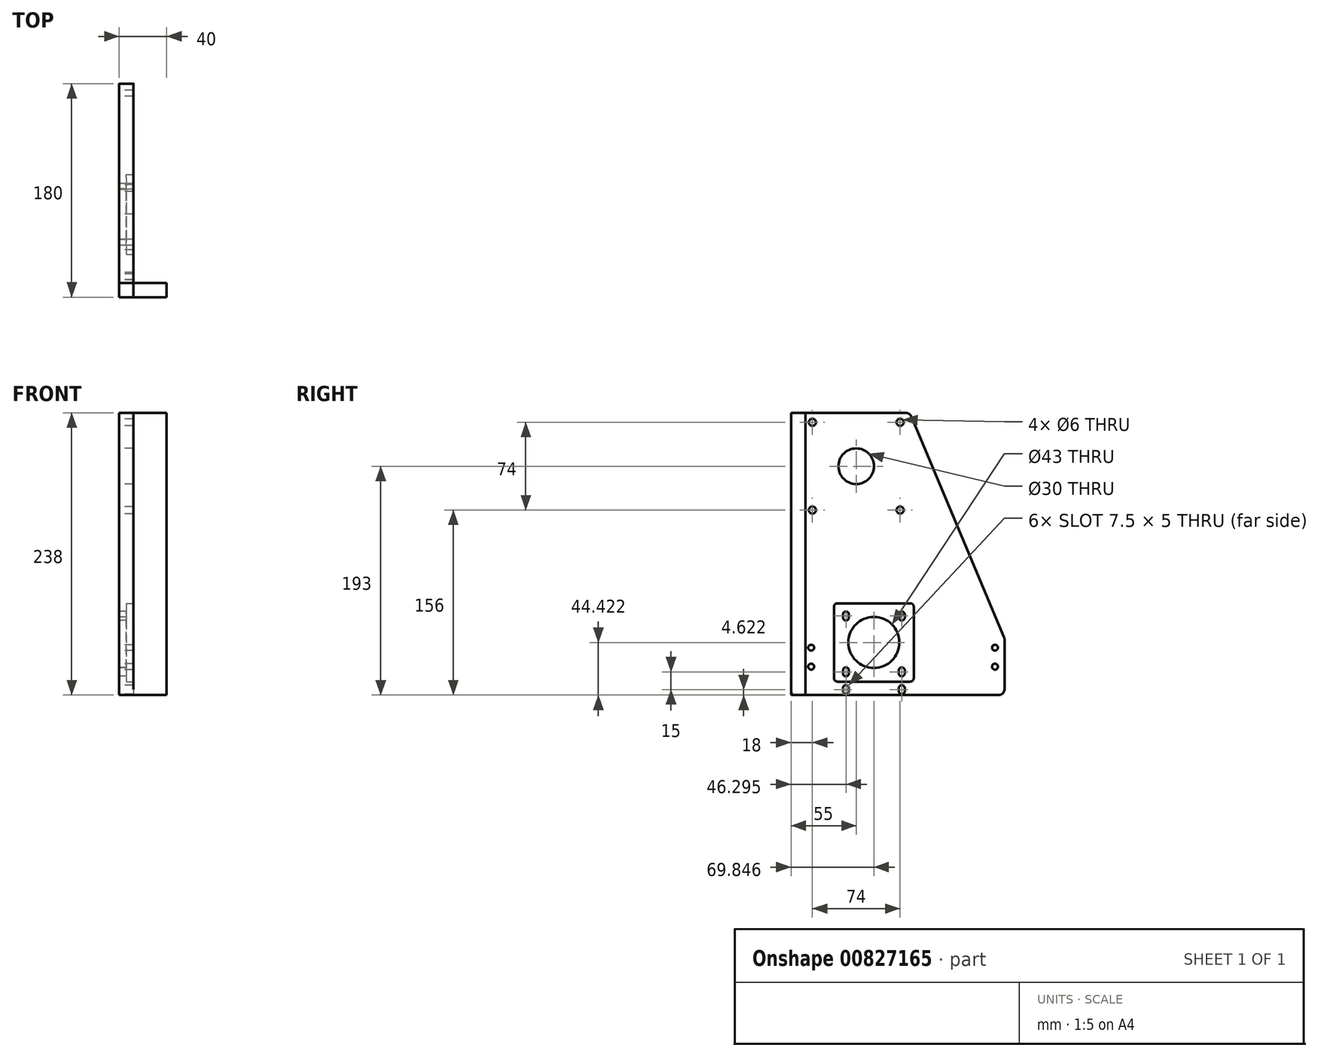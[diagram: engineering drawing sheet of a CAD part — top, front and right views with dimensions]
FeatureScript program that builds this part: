
annotation { "Feature Type Name" : "Feature", "Feature Type Description" : "" }
export const myFeature = defineFeature(function(context is Context, id is Id, definition is map)
    precondition{}
    {
        {
            var Q0;
            Q0=qCreatedBy(makeId("Right.planeOp"),FACE);
            var sketch = newSketch(context, id + "F0", { "sketchPlane" : qUnion([Q0])});
            skLineSegment(sketch, "E0", {"start": v(-40, 70) * mm, "end": v(-40, -155) * mm});
            skLineSegment(sketch, "E1", {"start": v(140, -168) * mm, "end": v(140, -120) * mm});
            skLineSegment(sketch, "E2", {"start": v(140, -120) * mm, "end": v(60, 70) * mm});
            skLineSegment(sketch, "E3", {"start": v(-40, 70) * mm, "end": v(60, 70) * mm});
            skLineSegment(sketch, "E4", {"start": v(0.37, 70) * mm, "end": v(-40, 70) * mm, "construction": true});
            skLineSegment(sketch, "E5", {"start": v(-153.96, -155) * mm, "end": v(265.91, -155) * mm, "construction": true});
            skLineSegment(sketch, "E6.top", {"start": v(6.3, -147.13) * mm, "end": v(53.4, -147.13) * mm, "construction": true});
            skLineSegment(sketch, "E7", {"start": v(29.85, -123.58) * mm, "end": v(29.85, -139.58) * mm, "construction": true});
            skLineSegment(sketch, "E8.bottom", {"start": v(60, 70) * mm, "end": v(-30, 70) * mm, "construction": true});
            skLineSegment(sketch, "E8.top", {"start": v(60, -20) * mm, "end": v(-30, -20) * mm, "construction": true});
            skLineSegment(sketch, "E8.left", {"start": v(60, 70) * mm, "end": v(60, -20) * mm, "construction": true});
            skLineSegment(sketch, "E8.right", {"start": v(-30, 70) * mm, "end": v(-30, -20) * mm, "construction": true});
            skLineSegment(sketch, "E9", {"start": v(-30, 70) * mm, "end": v(-30, 62) * mm, "construction": true});
            skLineSegment(sketch, "E10", {"start": v(-30, 62) * mm, "end": v(-22, 62) * mm, "construction": true});
            skCircle(sketch, "E11", {"center": v(-22, 62) * mm, "radius": 3 * mm});
            skCircle(sketch, "E12.0.1.0", {"center": v(-22, -12) * mm, "radius": 3 * mm});
            skCircle(sketch, "E12.1.0.0", {"center": v(52, 62) * mm, "radius": 3 * mm});
            skCircle(sketch, "E12.1.1.0", {"center": v(52, -12) * mm, "radius": 3 * mm});
            skLineSegment(sketch, "E12.direction1", {"start": v(-22, 62) * mm, "end": v(52, 62) * mm, "construction": true});
            skLineSegment(sketch, "E12.direction2", {"start": v(-22, 62) * mm, "end": v(-22, -12) * mm, "construction": true});
            skLineSegment(sketch, "E13", {"start": v(0, 0) * mm, "end": v(-30, 0) * mm, "construction": true});
            skLineSegment(sketch, "E14", {"start": v(-30, -20) * mm, "end": v(-30, 0) * mm, "construction": true});
            skLineSegment(sketch, "E15.bottom", {"start": v(-15.26, 54.8) * mm, "end": v(45.26, 54.8) * mm, "construction": true});
            skLineSegment(sketch, "E15.top", {"start": v(-15.26, -4.8) * mm, "end": v(45.26, -4.8) * mm, "construction": true});
            skLineSegment(sketch, "E15.left", {"start": v(-15.26, 54.8) * mm, "end": v(-15.26, -4.8) * mm, "construction": true});
            skLineSegment(sketch, "E15.right", {"start": v(45.26, 54.8) * mm, "end": v(45.26, -4.8) * mm, "construction": true});
            skLineSegment(sketch, "E16", {"start": v(0, 0) * mm, "end": v(0.37, 70) * mm, "construction": true});
            skLineSegment(sketch, "E17", {"start": v(52, -12) * mm, "end": v(-22, 62) * mm, "construction": true});
            skCircle(sketch, "E18", {"center": v(15, 25) * mm, "radius": 15 * mm});
            skLineSegment(sketch, "E19.bottom", {"start": v(-15.28, -29.16) * mm, "end": v(80.04, -29.16) * mm});
            skLineSegment(sketch, "E19.top", {"start": v(-15.28, -109.16) * mm, "end": v(113.72, -109.16) * mm});
            skLineSegment(sketch, "E19.left", {"start": v(-15.28, -29.16) * mm, "end": v(-15.28, -109.16) * mm});
            skLineSegment(sketch, "E20", {"start": v(80.04, -29.16) * mm, "end": v(113.72, -109.16) * mm});
            skLineSegment(sketch, "E21", {"start": v(132, -122.13) * mm, "end": v(132, -167.13) * mm, "construction": true});
            skLineSegment(sketch, "E22", {"start": v(132, -155) * mm, "end": v(132, -144) * mm, "construction": true});
            skCircle(sketch, "E23", {"center": v(132, -144) * mm, "radius": 11 * mm, "construction": true});
            skCircle(sketch, "E24", {"center": v(132, -144) * mm, "radius": 2.5 * mm});
            skLineSegment(sketch, "E25", {"start": v(132, -144) * mm, "end": v(132, -128) * mm, "construction": true});
            skCircle(sketch, "E26", {"center": v(132, -128) * mm, "radius": 2.5 * mm});
            skLineSegment(sketch, "E27", {"start": v(140, -155) * mm, "end": v(132, -155) * mm, "construction": true});
            skLineSegment(sketch, "E28", {"start": v(-40, -155) * mm, "end": v(-23, -155) * mm, "construction": true});
            skLineSegment(sketch, "E29", {"start": v(-23, -155) * mm, "end": v(-23, -144) * mm, "construction": true});
            skLineSegment(sketch, "E30", {"start": v(-23, -122.13) * mm, "end": v(-23, -167.13) * mm, "construction": true});
            skCircle(sketch, "E31", {"center": v(-23, -144) * mm, "radius": 11 * mm, "construction": true});
            skCircle(sketch, "E32", {"center": v(-23, -144) * mm, "radius": 2.5 * mm});
            skLineSegment(sketch, "E33", {"start": v(-23, -144) * mm, "end": v(-23, -128) * mm, "construction": true});
            skCircle(sketch, "E34", {"center": v(-23, -128) * mm, "radius": 2.5 * mm});
            skLineSegment(sketch, "E35", {"start": v(265.91, -188) * mm, "end": v(-153.96, -188) * mm, "construction": true});
            skLineSegment(sketch, "E36", {"start": v(140, -188) * mm, "end": v(140, -176) * mm, "construction": true});
            skLineSegment(sketch, "E37", {"start": v(265.91, -176) * mm, "end": v(-153.96, -176) * mm, "construction": true});
            skLineSegment(sketch, "E38", {"start": v(-19.95, -188) * mm, "end": v(100.05, -188) * mm});
            skLineSegment(sketch, "E39", {"start": v(-153.96, -123.47) * mm, "end": v(-153.96, -187.78) * mm, "construction": true});
            skLineSegment(sketch, "E40", {"start": v(265.91, -147.12) * mm, "end": v(265.91, -199.13) * mm, "construction": true});
            skLineSegment(sketch, "E41", {"start": v(140, -155) * mm, "end": v(140, -168) * mm});
            skLineSegment(sketch, "E42", {"start": v(140, -168) * mm, "end": v(-40, -168) * mm});
            skLineSegment(sketch, "E43", {"start": v(-40, -155) * mm, "end": v(-40, -168) * mm});
            skCircle(sketch, "E44", {"center": v(6.3, -147.13) * mm, "radius": 2.5 * mm});
            skCircle(sketch, "E45", {"center": v(53.4, -147.13) * mm, "radius": 2.5 * mm});
            skCircle(sketch, "E46", {"center": v(29.85, -123.58) * mm, "radius": 21.5 * mm});
            skLineSegment(sketch, "E47.bottom", {"start": v(6.3, -100.03) * mm, "end": v(53.4, -100.03) * mm, "construction": true});
            skLineSegment(sketch, "E47.left", {"start": v(6.3, -100.03) * mm, "end": v(6.3, -147.13) * mm, "construction": true});
            skLineSegment(sketch, "E47.right", {"start": v(53.4, -100.03) * mm, "end": v(53.4, -147.13) * mm, "construction": true});
            skCircle(sketch, "E48", {"center": v(29.85, -123.58) * mm, "radius": 6.5 * mm, "construction": true});
            skLineSegment(sketch, "E49", {"start": v(6.3, -100.03) * mm, "end": v(53.4, -147.13) * mm, "construction": true});
            skArc(sketch, "E50", {"start": v(3.8, -102.53) * mm, "mid": v(6.3, -105.03) * mm, "end": v(8.8, -102.53) * mm});
            skLineSegment(sketch, "E51", {"start": v(3.8, -100.03) * mm, "end": v(3.8, -102.53) * mm});
            skLineSegment(sketch, "E52", {"start": v(8.8, -100.03) * mm, "end": v(8.8, -102.53) * mm});
            skArc(sketch, "E53.trimOffspring", {"start": v(8.8, -100.03) * mm, "mid": v(6.3, -97.53) * mm, "end": v(3.8, -100.03) * mm});
            skArc(sketch, "E54", {"start": v(50.88, -102.52) * mm, "mid": v(53.38, -105.02) * mm, "end": v(55.88, -102.52) * mm});
            skLineSegment(sketch, "E55", {"start": v(50.88, -100.02) * mm, "end": v(50.88, -102.52) * mm});
            skLineSegment(sketch, "E56", {"start": v(55.88, -100.02) * mm, "end": v(55.88, -102.52) * mm});
            skArc(sketch, "E57.trimOffspring", {"start": v(55.88, -100.02) * mm, "mid": v(53.38, -97.52) * mm, "end": v(50.88, -100.02) * mm});
            skArc(sketch, "E58", {"start": v(50.9, -149.63) * mm, "mid": v(53.4, -152.13) * mm, "end": v(55.9, -149.63) * mm});
            skLineSegment(sketch, "E59", {"start": v(50.9, -147.13) * mm, "end": v(50.9, -149.63) * mm});
            skLineSegment(sketch, "E60", {"start": v(55.9, -147.13) * mm, "end": v(55.9, -149.63) * mm});
            skArc(sketch, "E61.trimOffspring", {"start": v(55.9, -147.13) * mm, "mid": v(53.4, -144.63) * mm, "end": v(50.9, -147.13) * mm});
            skArc(sketch, "E62", {"start": v(3.8, -149.63) * mm, "mid": v(6.3, -152.13) * mm, "end": v(8.8, -149.63) * mm});
            skLineSegment(sketch, "E63", {"start": v(3.8, -147.13) * mm, "end": v(3.8, -149.63) * mm});
            skLineSegment(sketch, "E64", {"start": v(8.8, -147.13) * mm, "end": v(8.8, -149.63) * mm});
            skArc(sketch, "E65.trimOffspring", {"start": v(8.8, -147.13) * mm, "mid": v(6.3, -144.63) * mm, "end": v(3.8, -147.13) * mm});
            skLineSegment(sketch, "E66", {"start": v(29.85, -123.58) * mm, "end": v(29.85, -126.08) * mm, "construction": true});
            skCircle(sketch, "E67", {"center": v(6.3, -147.13) * mm, "radius": 15 * mm, "construction": true});
            skCircle(sketch, "E68", {"center": v(53.4, -147.13) * mm, "radius": 15 * mm, "construction": true});
            skPoint(sketch, "E69.visualSharp", {"position": v(-0.7, -166.75) * mm});
            skPoint(sketch, "E70.visualSharp", {"position": v(59.3, -166.75) * mm});
            skArc(sketch, "E71", {"start": v(3.8, -164.63) * mm, "mid": v(6.3, -167.13) * mm, "end": v(8.8, -164.63) * mm});
            skLineSegment(sketch, "E72", {"start": v(3.8, -162.13) * mm, "end": v(3.8, -164.63) * mm});
            skLineSegment(sketch, "E73", {"start": v(8.8, -162.13) * mm, "end": v(8.8, -164.63) * mm});
            skArc(sketch, "E74.trimOffspring", {"start": v(8.8, -162.13) * mm, "mid": v(6.3, -159.63) * mm, "end": v(3.8, -162.13) * mm});
            skArc(sketch, "E75", {"start": v(50.9, -164.63) * mm, "mid": v(53.4, -167.13) * mm, "end": v(55.9, -164.63) * mm});
            skLineSegment(sketch, "E76", {"start": v(50.9, -162.13) * mm, "end": v(50.9, -164.63) * mm});
            skLineSegment(sketch, "E77", {"start": v(55.9, -162.13) * mm, "end": v(55.9, -164.63) * mm});
            skArc(sketch, "E78.trimOffspring", {"start": v(55.9, -162.13) * mm, "mid": v(53.4, -159.63) * mm, "end": v(50.9, -162.13) * mm});
            skLineSegment(sketch, "E79", {"start": v(55.9, -147.13) * mm, "end": v(55.9, -162.13) * mm, "construction": true});
            skLineSegment(sketch, "E80", {"start": v(23.35, -123.47) * mm, "end": v(22.64, -166.43) * mm, "construction": true});
            skLineSegment(sketch, "E81", {"start": v(36.34, -123.3) * mm, "end": v(36.34, -166.03) * mm, "construction": true});
            skSolve(sketch);
        }
        {
            var Q0;
            Q0=makeQuery(id+"F0.imprint","IMPRINT",FACE,{"disambiguationData":[TD([[makeQuery(id+"F0.imprint","IMPRINT",EDGE,{"derivedFrom":sQuery(id+"F0.wireOp",EDGE,"E0")}),1.0]])]});
            var Q1;
            Q1=makeQuery(id+"F0.imprint","IMPRINT",FACE,{"disambiguationData":[TD([[makeQuery(id+"F0.imprint","IMPRINT",EDGE,{"derivedFrom":sQuery(id+"F0.wireOp",EDGE,"E19.bottom")}),-1.0]])]});
            extrude(context, id + "F1", {"entities" : qUnion([Q0, Q1]), "depth" : 12 * mm, "offsetDistance" : 25 * mm});
        }
        {
            var Q0;
            Q0=makeQuery(id+"F1.opExtrude","SWEPT_EDGE",EDGE,{"disambiguationData":[OSD([sQuery(id+"F0.wireOp",EDGE,"E2"),sQuery(id+"F0.wireOp",EDGE,"E3")])]});
            var Q1;
            Q1=makeQuery(id+"F1.opExtrude","SWEPT_EDGE",EDGE,{"disambiguationData":[OSD([sQuery(id+"F0.wireOp",EDGE,"E1"),sQuery(id+"F0.wireOp",EDGE,"E2")])]});
            var Q2;
            Q2=makeQuery(id+"F1.opExtrude","SWEPT_EDGE",EDGE,{"disambiguationData":[OSD([sQuery(id+"F0.wireOp",EDGE,"E41"),sQuery(id+"F0.wireOp",EDGE,"E42")])]});
            fillet(context, id + "F2", {"entities" : qUnion([Q0, Q1, Q2]), "radius" : 5 * mm, "tangentPropagation" : true, "allowEdgeOverflow" : false});
        }
        {
            var Q0;
            Q0=qCreatedBy(makeId("Right.planeOp"),FACE);
            var sketch = newSketch(context, id + "F3", { "sketchPlane" : qUnion([Q0])});
            skLineSegment(sketch, "E82.bottom", {"start": v(-40, 70) * mm, "end": v(-28, 70) * mm});
            skLineSegment(sketch, "E82.top", {"start": v(-40, -168) * mm, "end": v(-28, -168) * mm});
            skLineSegment(sketch, "E82.left", {"start": v(-28, 70) * mm, "end": v(-28, -168) * mm});
            skLineSegment(sketch, "E82.right", {"start": v(-40, 70) * mm, "end": v(-40, -168) * mm});
            skSolve(sketch);
        }
        {
            var Q0;
            Q0=makeQuery(id+"F3.imprint","IMPRINT",FACE,{"disambiguationData":[TD([[makeQuery(id+"F3.imprint","IMPRINT",EDGE,{"derivedFrom":sQuery(id+"F3.wireOp",EDGE,"E82.bottom")}),-1.0]])]});
            extrude(context, id + "F4", {"entities" : qUnion([Q0]), "depth" : 40 * mm, "offsetDistance" : 25 * mm});
        }
        {
            var Q0;
            Q0=makeQuery(id+"F1.opExtrude","CAP_FACE",FACE,{"disambiguationData":[OSD([sQuery(id+"F0.wireOp",EDGE,"E0"),sQuery(id+"F0.wireOp",EDGE,"E1"),sQuery(id+"F0.wireOp",EDGE,"E2"),sQuery(id+"F0.wireOp",EDGE,"E3"),sQuery(id+"F0.wireOp",EDGE,"E11"),sQuery(id+"F0.wireOp",EDGE,"E12.0.1.0"),sQuery(id+"F0.wireOp",EDGE,"E12.1.0.0"),sQuery(id+"F0.wireOp",EDGE,"E12.1.1.0"),sQuery(id+"F0.wireOp",EDGE,"E18"),sQuery(id+"F0.wireOp",EDGE,"E24"),sQuery(id+"F0.wireOp",EDGE,"E26"),sQuery(id+"F0.wireOp",EDGE,"E32"),sQuery(id+"F0.wireOp",EDGE,"E34"),sQuery(id+"F0.wireOp",EDGE,"E41"),sQuery(id+"F0.wireOp",EDGE,"E42"),sQuery(id+"F0.wireOp",EDGE,"E43"),sQuery(id+"F0.wireOp",EDGE,"E44"),sQuery(id+"F0.wireOp",EDGE,"E45"),sQuery(id+"F0.wireOp",EDGE,"E46"),sQuery(id+"F0.wireOp",EDGE,"E50"),sQuery(id+"F0.wireOp",EDGE,"E51"),sQuery(id+"F0.wireOp",EDGE,"E52"),sQuery(id+"F0.wireOp",EDGE,"E53.trimOffspring"),sQuery(id+"F0.wireOp",EDGE,"E54"),sQuery(id+"F0.wireOp",EDGE,"E55"),sQuery(id+"F0.wireOp",EDGE,"E56"),sQuery(id+"F0.wireOp",EDGE,"E57.trimOffspring"),sQuery(id+"F0.wireOp",EDGE,"E58"),sQuery(id+"F0.wireOp",EDGE,"E59"),sQuery(id+"F0.wireOp",EDGE,"E60"),sQuery(id+"F0.wireOp",EDGE,"E62"),sQuery(id+"F0.wireOp",EDGE,"E63"),sQuery(id+"F0.wireOp",EDGE,"E64")])],"isStart":false});
            var sketch = newSketch(context, id + "F5", { "sketchPlane" : qUnion([Q0])});
            skLineSegment(sketch, "E83.bottom", {"start": v(63.5, -90.56) * mm, "end": v(-3.82, -90.56) * mm});
            skLineSegment(sketch, "E83.top", {"start": v(63.5, -156.6) * mm, "end": v(-3.82, -156.6) * mm});
            skLineSegment(sketch, "E83.left", {"start": v(63.5, -90.56) * mm, "end": v(63.5, -156.6) * mm});
            skLineSegment(sketch, "E83.right", {"start": v(-3.82, -90.56) * mm, "end": v(-3.82, -156.6) * mm});
            skPoint(sketch, "E83.middle", {"position": v(29.85, -123.58) * mm});
            skSolve(sketch);
        }
        {
            var Q0;
            Q0=makeQuery(id+"F5.imprint","IMPRINT",FACE,{"disambiguationData":[TD([[makeQuery(id+"F5.imprint","IMPRINT",EDGE,{"derivedFrom":sQuery(id+"F5.wireOp",EDGE,"E83.bottom")}),1.0]])]});
            extrude(context, id + "F6", {"entities" : qUnion([Q0]), "operationType" : NewBodyOperationType.REMOVE, "oppositeDirection" : true, "depth" : 6 * mm, "offsetDistance" : 25 * mm});
        }
        {
            var Q0;
            Q0=makeQuery(id+"F6.boolean.opBoolean","COPY",EDGE,{"derivedFrom":makeQuery(id+"F6.opExtrude","SWEPT_EDGE",EDGE,{"disambiguationData":[OSD([sQuery(id+"F5.wireOp",EDGE,"E83.top"),sQuery(id+"F5.wireOp",EDGE,"E83.right")])]})});
            var Q1;
            Q1=makeQuery(id+"F6.boolean.opBoolean","COPY",EDGE,{"derivedFrom":makeQuery(id+"F6.opExtrude","SWEPT_EDGE",EDGE,{"disambiguationData":[OSD([sQuery(id+"F5.wireOp",EDGE,"E83.top"),sQuery(id+"F5.wireOp",EDGE,"E83.left")])]})});
            var Q2;
            Q2=makeQuery(id+"F6.boolean.opBoolean","COPY",EDGE,{"derivedFrom":makeQuery(id+"F6.opExtrude","SWEPT_EDGE",EDGE,{"disambiguationData":[OSD([sQuery(id+"F5.wireOp",EDGE,"E83.bottom"),sQuery(id+"F5.wireOp",EDGE,"E83.left")])]})});
            var Q3;
            Q3=makeQuery(id+"F6.boolean.opBoolean","COPY",EDGE,{"derivedFrom":makeQuery(id+"F6.opExtrude","SWEPT_EDGE",EDGE,{"disambiguationData":[OSD([sQuery(id+"F5.wireOp",EDGE,"E83.bottom"),sQuery(id+"F5.wireOp",EDGE,"E83.right")])]})});
            fillet(context, id + "F7", {"entities" : qUnion([Q0, Q1, Q2, Q3]), "radius" : 3 * mm, "tangentPropagation" : true, "allowEdgeOverflow" : false});
        }
    });
